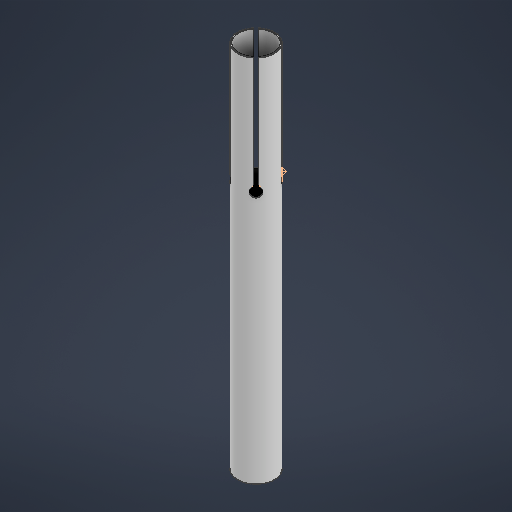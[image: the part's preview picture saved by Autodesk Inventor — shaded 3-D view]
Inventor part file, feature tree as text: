
AUTODESK INVENTOR PART (.ipt)
format: ipt  version: 2025 (Build 290162010, 162A)  size: 285,696 bytes
history: native  units: mm
features: extrude x3, sketch x3, other x2, plane x1, fillet x1, mirror x1
ambient origin geometry x8: Origin, YZ Plane, XZ Plane, XY Plane, X Axis, Y Axis, Z Axis, Center Point
bodies: Solid1 (feature_tree)
feature tree (11):
  extrude  "Extrusion1"  Depth=2.54mm
  extrude  "Extrusion2"  TaperAngle=45.0deg  [1 undecoded]
  other  "Work Point1"
  other  "Work Point2"
  plane  "Work Plane1"
  extrude  "Extrusion3"  Depth=6.25mm
  fillet  "Fillet1"  Radius=3.5mm
  mirror  "Mirror1"
  sketch  "Sketch1"  dims[d0=76.2mm d1=2.54mm]
  sketch  "Sketch2"  dims[d2=762.0mm d3=0.0mm d4=45.0deg]
  sketch  "Sketch3"  dims[d5=3.5mm d6=3.5mm d7=3.5mm d8=3.5mm d9=3.5mm d10=3.5mm d11=230.2mm d12=0.0mm d13=10.0mm d14=20.0mm d15=230.2mm d16=0.0mm d17=6.25mm]
note: 1 required parameter value undecoded (feature->parameter linkage not recoverable at this tier; creation-order binding heuristic only, values carry confidence <= 0.55)
